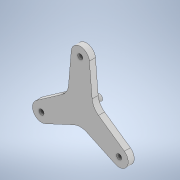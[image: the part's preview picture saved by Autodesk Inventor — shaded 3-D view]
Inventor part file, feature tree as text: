
AUTODESK INVENTOR PART (.ipt)
format: ipt  version: 2020 (Build 240168000, 168)  size: 166,912 bytes
history: native  units: mm
features: sketch x2, revolve x1, fillet x1, extrude x1, pattern_circular x1
ambient origin geometry x8: Origin, YZ Plane, XZ Plane, XY Plane, X Axis, Y Axis, Z Axis, Center Point
bodies: Solid1 (feature_tree)
feature tree (6):
  revolve  "Revolution1"  [1 undecoded]
  fillet  "Fillet1"  [1 undecoded]
  extrude  "Extrusion1"  Depth=11.0mm
  pattern_circular  "Circular Pattern1"  [2 undecoded]
  sketch  "Sketch1"  dims[d0=2.5mm d1=5.0mm d2=90.0deg]
  sketch  "Sketch2"  dims[d3=2.0mm d4=45.0mm d5=11.0mm d6=15.0mm d7=120.0deg d8=120.0deg d9=60.0deg d10=60.0deg d11=37.075mm d12=25.0mm d13=0.872665mm d14=0.0mm d15=0.0mm d16=30.0mm d17=360.0deg d19=4.2mm]
note: 4 required parameter values undecoded (feature->parameter linkage not recoverable at this tier; creation-order binding heuristic only, values carry confidence <= 0.55)